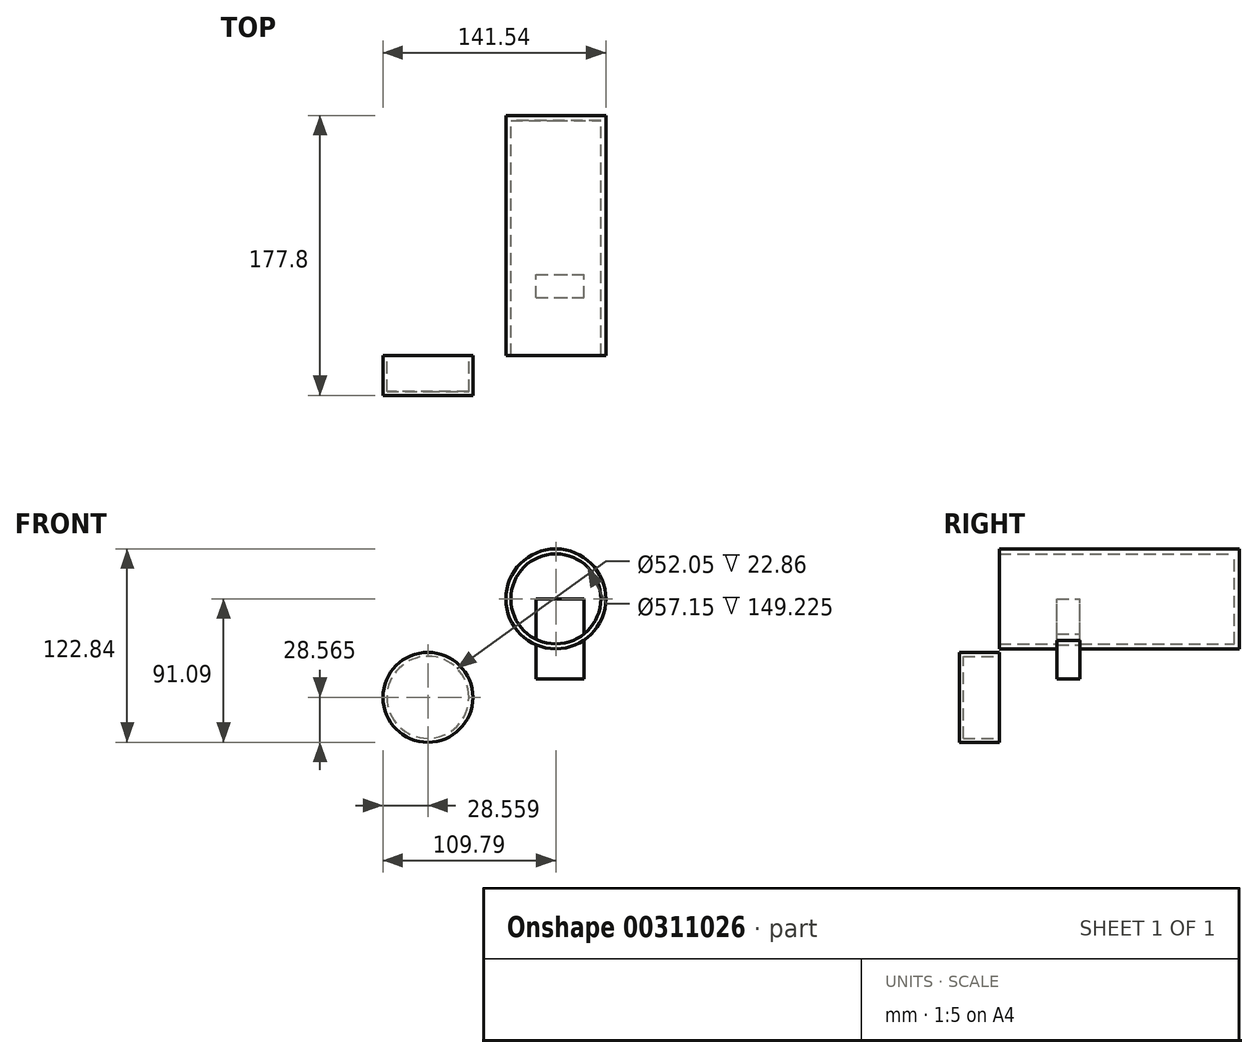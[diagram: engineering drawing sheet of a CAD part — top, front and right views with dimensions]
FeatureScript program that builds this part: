
annotation { "Feature Type Name" : "Feature", "Feature Type Description" : "" }
export const myFeature = defineFeature(function(context is Context, id is Id, definition is map)
    precondition{}
    {
        {
            var Q0;
            Q0=qCreatedBy(makeId("Front.planeOp"),FACE);
            var sketch = newSketch(context, id + "F0", { "sketchPlane" : qUnion([Q0])});
            skCircle(sketch, "E0", {"center": v(0, 0) * mm, "radius": 31.75 * mm});
            skCircle(sketch, "E1", {"center": v(0, 0) * mm, "radius": 28.58 * mm});
            skSolve(sketch);
        }
        {
            var Q0;
            Q0=makeQuery(id+"F0.imprint","IMPRINT",FACE,{"disambiguationData":[TD([[makeQuery(id+"F0.imprint","IMPRINT",EDGE,{"derivedFrom":sQuery(id+"F0.wireOp",EDGE,"E1")}),1.0]])]});
            extrude(context, id + "F1", {"entities" : qUnion([Q0]), "depth" : 3.17 * mm});
        }
        {
            var Q0;
            Q0=makeQuery(id+"F0.imprint","IMPRINT",FACE,{"disambiguationData":[TD([[makeQuery(id+"F0.imprint","IMPRINT",EDGE,{"derivedFrom":sQuery(id+"F0.wireOp",EDGE,"E0")}),1.0]])]});
            extrude(context, id + "F2", {"entities" : qUnion([Q0]), "operationType" : NewBodyOperationType.ADD, "depth" : 152.4 * mm});
        }
        {
            var Q0;
            Q0=makeQuery(id+"F2.opExtrude","CAP_FACE",FACE,{"disambiguationData":[OSD([sQuery(id+"F0.wireOp",EDGE,"E0"),sQuery(id+"F0.wireOp",EDGE,"E1")])],"isStart":false});
            var sketch = newSketch(context, id + "F3", { "sketchPlane" : qUnion([Q0])});
            skCircle(sketch, "E2", {"center": v(-81.23, -62.53) * mm, "radius": 33.02 * mm});
            skCircle(sketch, "E3", {"center": v(-81.23, -62.53) * mm, "radius": 28.56 * mm});
            skSolve(sketch);
        }
        {
            var Q0;
            Q0=makeQuery(id+"F3.imprint","IMPRINT",FACE,{"disambiguationData":[TD([[makeQuery(id+"F3.imprint","IMPRINT",EDGE,{"derivedFrom":sQuery(id+"F3.wireOp",EDGE,"E3")}),1.0]])]});
            extrude(context, id + "F4", {"entities" : qUnion([Q0]), "depth" : 25.4 * mm});
        }
        {
            var Q0;
            Q0=makeQuery(id+"F4.opExtrude","CAP_FACE",FACE,{"disambiguationData":[OSD([sQuery(id+"F3.wireOp",EDGE,"E3")])],"isStart":true});
            shell(context, id + "F5", {"entities" : qUnion([Q0]), "thickness" : 2.54 * mm});
        }
        {
            var Q0;
            Q0=qCreatedBy(makeId("Top.planeOp"),FACE);
            var sketch = newSketch(context, id + "F6", { "sketchPlane" : qUnion([Q0])});
            skLineSegment(sketch, "E4.bottom", {"start": v(-12.55, -115.68) * mm, "end": v(17.81, -115.68) * mm});
            skLineSegment(sketch, "E4.top", {"start": v(-12.55, -101.08) * mm, "end": v(17.81, -101.08) * mm});
            skLineSegment(sketch, "E4.left", {"start": v(-12.55, -115.68) * mm, "end": v(-12.55, -101.08) * mm});
            skLineSegment(sketch, "E4.right", {"start": v(17.81, -115.68) * mm, "end": v(17.81, -101.08) * mm});
            skSolve(sketch);
        }
        {
            var Q0;
            Q0 = qSketchRegion(id + "F6", true);
            extrude(context, id + "F7", {"entities" : qUnion([Q0]), "operationType" : NewBodyOperationType.ADD, "oppositeDirection" : true, "depth" : 50.8 * mm});
        }
    });
